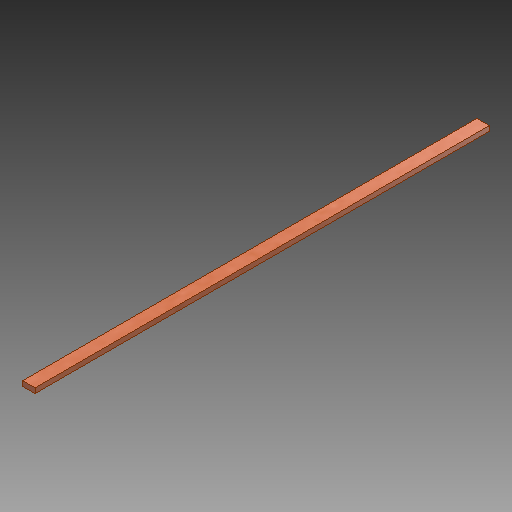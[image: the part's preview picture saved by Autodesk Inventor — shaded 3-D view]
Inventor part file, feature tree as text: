
AUTODESK INVENTOR PART (.ipt)
format: ipt  version: 2018 (Build 220112000, 112)  size: 88,064 bytes
history: native  units: mm
features: extrude x1
ambient origin geometry x8: Origin, YZ Plane, XZ Plane, XY Plane, X Axis, Y Axis, Z Axis, Center Point
bodies: Volumenkörper1 (feature_tree)
feature tree (1):
  extrude  "Extrusion1"  Depth=3.0mm
